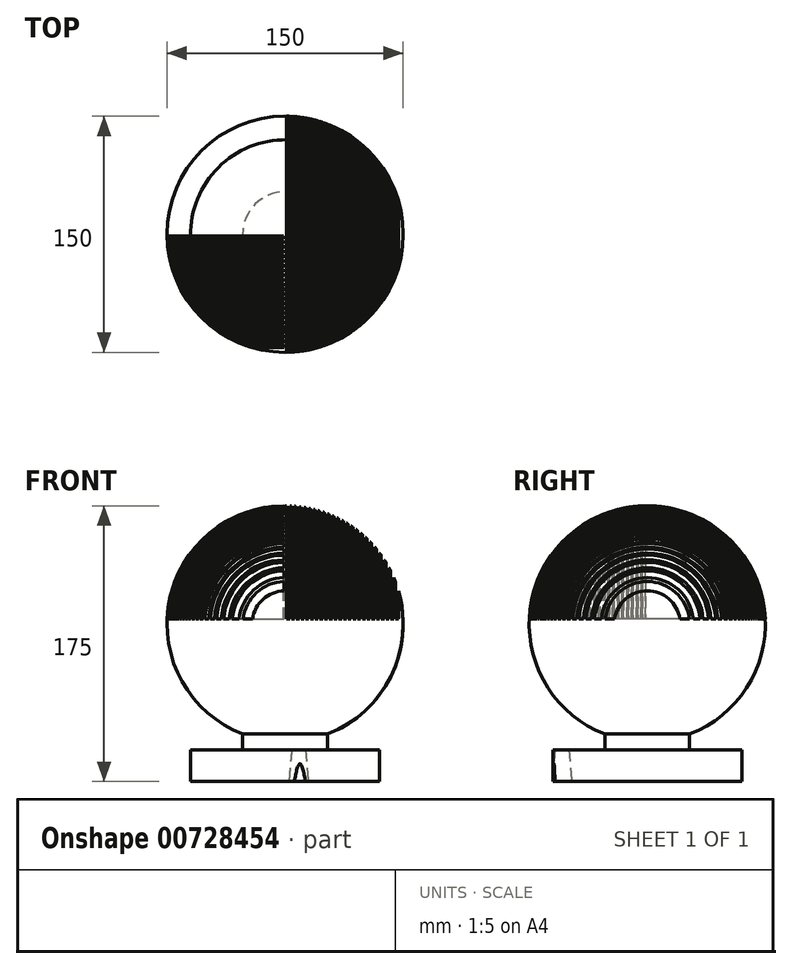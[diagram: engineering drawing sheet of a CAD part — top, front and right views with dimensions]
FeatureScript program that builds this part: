
annotation { "Feature Type Name" : "Feature", "Feature Type Description" : "" }
export const myFeature = defineFeature(function(context is Context, id is Id, definition is map)
    precondition{}
    {
        {
            var Q0;
            Q0=qCreatedBy(makeId("Front.planeOp"),FACE);
            var sketch = newSketch(context, id + "F0", { "sketchPlane" : qUnion([Q0])});
            skArc(sketch, "E0", {"start": v(26.93, -70) * mm, "mid": v(73.74, 13.7) * mm, "end": v(0, 75) * mm});
            skLineSegment(sketch, "E1", {"start": v(0, 75) * mm, "end": v(0, -100) * mm});
            skLineSegment(sketch, "E2", {"start": v(0, -100) * mm, "end": v(60, -100) * mm});
            skLineSegment(sketch, "E3", {"start": v(60, -100) * mm, "end": v(60, -80) * mm});
            skLineSegment(sketch, "E4", {"start": v(60, -80) * mm, "end": v(26.93, -80) * mm});
            skLineSegment(sketch, "E5", {"start": v(26.93, -70) * mm, "end": v(26.93, -80) * mm});
            skPoint(sketch, "E6.orphan", {"position": v(0, 81.47) * mm});
            skSolve(sketch);
        }
        {
            var Q0;
            Q0=makeQuery(id+"F0.imprint","IMPRINT",FACE,{"disambiguationData":[TD([[makeQuery(id+"F0.imprint","IMPRINT",EDGE,{"derivedFrom":sQuery(id+"F0.wireOp",EDGE,"E0")}),1.0]])]});
            var Q1;
            Q1=sQuery(id+"F0.wireOp",EDGE,"E1");
            revolve(context, id + "F1", {"surfaceOperationType" : NewSurfaceOperationType.NEW, "entities" : qUnion([Q0]), "axis" : qUnion([Q1]), "revolveType" : RevolveType.FULL});
        }
        {
            var Q0;
            Q0=qCreatedBy(makeId("Top.planeOp"),FACE);
            cPlane(context, id + "F2", {"entities" : qUnion([Q0]), "cplaneType" : CPlaneType.OFFSET, "offset" : 75 * mm, "width" : 150 * mm, "height" : 150 * mm});
        }
        {
            var Q0;
            Q0=qCreatedBy(id+"F2.planeOp",FACE);
            var sketch = newSketch(context, id + "F3", { "sketchPlane" : qUnion([Q0])});
            skLineSegment(sketch, "E7.bottom", {"start": v(1, 100) * mm, "end": v(3, 100) * mm});
            skLineSegment(sketch, "E7.top", {"start": v(1, -80) * mm, "end": v(3, -80) * mm});
            skLineSegment(sketch, "E7.left", {"start": v(1, 100) * mm, "end": v(1, -80) * mm});
            skLineSegment(sketch, "E7.right", {"start": v(3, 100) * mm, "end": v(3, -80) * mm});
            skLineSegment(sketch, "E8.1.0.0", {"start": v(6, 100) * mm, "end": v(6, -80) * mm});
            skLineSegment(sketch, "E8.1.0.1", {"start": v(4, 100) * mm, "end": v(4, -80) * mm});
            skLineSegment(sketch, "E8.1.0.2", {"start": v(4, -80) * mm, "end": v(6, -80) * mm});
            skLineSegment(sketch, "E8.1.0.3", {"start": v(4, 100) * mm, "end": v(6, 100) * mm});
            skLineSegment(sketch, "E8.2.0.0", {"start": v(9, 100) * mm, "end": v(9, -80) * mm});
            skLineSegment(sketch, "E8.2.0.1", {"start": v(7, 100) * mm, "end": v(7, -80) * mm});
            skLineSegment(sketch, "E8.2.0.2", {"start": v(7, -80) * mm, "end": v(9, -80) * mm});
            skLineSegment(sketch, "E8.2.0.3", {"start": v(7, 100) * mm, "end": v(9, 100) * mm});
            skLineSegment(sketch, "E8.3.0.0", {"start": v(12, 100) * mm, "end": v(12, -80) * mm});
            skLineSegment(sketch, "E8.3.0.1", {"start": v(10, 100) * mm, "end": v(10, -80) * mm});
            skLineSegment(sketch, "E8.3.0.2", {"start": v(10, -80) * mm, "end": v(12, -80) * mm});
            skLineSegment(sketch, "E8.3.0.3", {"start": v(10, 100) * mm, "end": v(12, 100) * mm});
            skLineSegment(sketch, "E8.4.0.0", {"start": v(15, 100) * mm, "end": v(15, -80) * mm});
            skLineSegment(sketch, "E8.4.0.1", {"start": v(13, 100) * mm, "end": v(13, -80) * mm});
            skLineSegment(sketch, "E8.4.0.2", {"start": v(13, -80) * mm, "end": v(15, -80) * mm});
            skLineSegment(sketch, "E8.4.0.3", {"start": v(13, 100) * mm, "end": v(15, 100) * mm});
            skLineSegment(sketch, "E8.5.0.0", {"start": v(18, 100) * mm, "end": v(18, -80) * mm});
            skLineSegment(sketch, "E8.5.0.1", {"start": v(16, 100) * mm, "end": v(16, -80) * mm});
            skLineSegment(sketch, "E8.5.0.2", {"start": v(16, -80) * mm, "end": v(18, -80) * mm});
            skLineSegment(sketch, "E8.5.0.3", {"start": v(16, 100) * mm, "end": v(18, 100) * mm});
            skLineSegment(sketch, "E8.6.0.0", {"start": v(21, 100) * mm, "end": v(21, -80) * mm});
            skLineSegment(sketch, "E8.6.0.1", {"start": v(19, 100) * mm, "end": v(19, -80) * mm});
            skLineSegment(sketch, "E8.6.0.2", {"start": v(19, -80) * mm, "end": v(21, -80) * mm});
            skLineSegment(sketch, "E8.6.0.3", {"start": v(19, 100) * mm, "end": v(21, 100) * mm});
            skLineSegment(sketch, "E8.7.0.0", {"start": v(24, 100) * mm, "end": v(24, -80) * mm});
            skLineSegment(sketch, "E8.7.0.1", {"start": v(22, 100) * mm, "end": v(22, -80) * mm});
            skLineSegment(sketch, "E8.7.0.2", {"start": v(22, -80) * mm, "end": v(24, -80) * mm});
            skLineSegment(sketch, "E8.7.0.3", {"start": v(22, 100) * mm, "end": v(24, 100) * mm});
            skLineSegment(sketch, "E8.8.0.0", {"start": v(27, 100) * mm, "end": v(27, -80) * mm});
            skLineSegment(sketch, "E8.8.0.1", {"start": v(25, 100) * mm, "end": v(25, -80) * mm});
            skLineSegment(sketch, "E8.8.0.2", {"start": v(25, -80) * mm, "end": v(27, -80) * mm});
            skLineSegment(sketch, "E8.8.0.3", {"start": v(25, 100) * mm, "end": v(27, 100) * mm});
            skLineSegment(sketch, "E8.9.0.0", {"start": v(30, 100) * mm, "end": v(30, -80) * mm});
            skLineSegment(sketch, "E8.9.0.1", {"start": v(28, 100) * mm, "end": v(28, -80) * mm});
            skLineSegment(sketch, "E8.9.0.2", {"start": v(28, -80) * mm, "end": v(30, -80) * mm});
            skLineSegment(sketch, "E8.9.0.3", {"start": v(28, 100) * mm, "end": v(30, 100) * mm});
            skLineSegment(sketch, "E8.10.0.0", {"start": v(33, 100) * mm, "end": v(33, -80) * mm});
            skLineSegment(sketch, "E8.10.0.1", {"start": v(31, 100) * mm, "end": v(31, -80) * mm});
            skLineSegment(sketch, "E8.10.0.2", {"start": v(31, -80) * mm, "end": v(33, -80) * mm});
            skLineSegment(sketch, "E8.10.0.3", {"start": v(31, 100) * mm, "end": v(33, 100) * mm});
            skLineSegment(sketch, "E8.11.0.0", {"start": v(36, 100) * mm, "end": v(36, -80) * mm});
            skLineSegment(sketch, "E8.11.0.1", {"start": v(34, 100) * mm, "end": v(34, -80) * mm});
            skLineSegment(sketch, "E8.11.0.2", {"start": v(34, -80) * mm, "end": v(36, -80) * mm});
            skLineSegment(sketch, "E8.11.0.3", {"start": v(34, 100) * mm, "end": v(36, 100) * mm});
            skLineSegment(sketch, "E8.12.0.0", {"start": v(39, 100) * mm, "end": v(39, -80) * mm});
            skLineSegment(sketch, "E8.12.0.1", {"start": v(37, 100) * mm, "end": v(37, -80) * mm});
            skLineSegment(sketch, "E8.12.0.2", {"start": v(37, -80) * mm, "end": v(39, -80) * mm});
            skLineSegment(sketch, "E8.12.0.3", {"start": v(37, 100) * mm, "end": v(39, 100) * mm});
            skLineSegment(sketch, "E8.13.0.0", {"start": v(42, 100) * mm, "end": v(42, -80) * mm});
            skLineSegment(sketch, "E8.13.0.1", {"start": v(40, 100) * mm, "end": v(40, -80) * mm});
            skLineSegment(sketch, "E8.13.0.2", {"start": v(40, -80) * mm, "end": v(42, -80) * mm});
            skLineSegment(sketch, "E8.13.0.3", {"start": v(40, 100) * mm, "end": v(42, 100) * mm});
            skLineSegment(sketch, "E8.14.0.0", {"start": v(45, 100) * mm, "end": v(45, -80) * mm});
            skLineSegment(sketch, "E8.14.0.1", {"start": v(43, 100) * mm, "end": v(43, -80) * mm});
            skLineSegment(sketch, "E8.14.0.2", {"start": v(43, -80) * mm, "end": v(45, -80) * mm});
            skLineSegment(sketch, "E8.14.0.3", {"start": v(43, 100) * mm, "end": v(45, 100) * mm});
            skLineSegment(sketch, "E8.15.0.0", {"start": v(48, 100) * mm, "end": v(48, -80) * mm});
            skLineSegment(sketch, "E8.15.0.1", {"start": v(46, 100) * mm, "end": v(46, -80) * mm});
            skLineSegment(sketch, "E8.15.0.2", {"start": v(46, -80) * mm, "end": v(48, -80) * mm});
            skLineSegment(sketch, "E8.15.0.3", {"start": v(46, 100) * mm, "end": v(48, 100) * mm});
            skLineSegment(sketch, "E8.16.0.0", {"start": v(51, 100) * mm, "end": v(51, -80) * mm});
            skLineSegment(sketch, "E8.16.0.1", {"start": v(49, 100) * mm, "end": v(49, -80) * mm});
            skLineSegment(sketch, "E8.16.0.2", {"start": v(49, -80) * mm, "end": v(51, -80) * mm});
            skLineSegment(sketch, "E8.16.0.3", {"start": v(49, 100) * mm, "end": v(51, 100) * mm});
            skLineSegment(sketch, "E8.17.0.0", {"start": v(54, 100) * mm, "end": v(54, -80) * mm});
            skLineSegment(sketch, "E8.17.0.1", {"start": v(52, 100) * mm, "end": v(52, -80) * mm});
            skLineSegment(sketch, "E8.17.0.2", {"start": v(52, -80) * mm, "end": v(54, -80) * mm});
            skLineSegment(sketch, "E8.17.0.3", {"start": v(52, 100) * mm, "end": v(54, 100) * mm});
            skLineSegment(sketch, "E8.direction1", {"start": v(1, -80) * mm, "end": v(4, -80) * mm, "construction": true});
            skLineSegment(sketch, "E9.0.18.0", {"start": v(57, 100) * mm, "end": v(57, -80) * mm});
            skLineSegment(sketch, "E9.3.18.0", {"start": v(55, 100) * mm, "end": v(55, -80) * mm});
            skLineSegment(sketch, "E9.6.18.0", {"start": v(55, -80) * mm, "end": v(57, -80) * mm});
            skLineSegment(sketch, "E9.9.18.0", {"start": v(55, 100) * mm, "end": v(57, 100) * mm});
            skLineSegment(sketch, "E9.0.19.0", {"start": v(60, 100) * mm, "end": v(60, -80) * mm});
            skLineSegment(sketch, "E9.3.19.0", {"start": v(58, 100) * mm, "end": v(58, -80) * mm});
            skLineSegment(sketch, "E9.6.19.0", {"start": v(58, -80) * mm, "end": v(60, -80) * mm});
            skLineSegment(sketch, "E9.9.19.0", {"start": v(58, 100) * mm, "end": v(60, 100) * mm});
            skLineSegment(sketch, "E9.0.20.0", {"start": v(63, 100) * mm, "end": v(63, -80) * mm});
            skLineSegment(sketch, "E9.3.20.0", {"start": v(61, 100) * mm, "end": v(61, -80) * mm});
            skLineSegment(sketch, "E9.6.20.0", {"start": v(61, -80) * mm, "end": v(63, -80) * mm});
            skLineSegment(sketch, "E9.9.20.0", {"start": v(61, 100) * mm, "end": v(63, 100) * mm});
            skLineSegment(sketch, "E9.0.21.0", {"start": v(66, 100) * mm, "end": v(66, -80) * mm});
            skLineSegment(sketch, "E9.3.21.0", {"start": v(64, 100) * mm, "end": v(64, -80) * mm});
            skLineSegment(sketch, "E9.6.21.0", {"start": v(64, -80) * mm, "end": v(66, -80) * mm});
            skLineSegment(sketch, "E9.9.21.0", {"start": v(64, 100) * mm, "end": v(66, 100) * mm});
            skLineSegment(sketch, "E9.0.22.0", {"start": v(69, 100) * mm, "end": v(69, -80) * mm});
            skLineSegment(sketch, "E9.3.22.0", {"start": v(67, 100) * mm, "end": v(67, -80) * mm});
            skLineSegment(sketch, "E9.6.22.0", {"start": v(67, -80) * mm, "end": v(69, -80) * mm});
            skLineSegment(sketch, "E9.9.22.0", {"start": v(67, 100) * mm, "end": v(69, 100) * mm});
            skLineSegment(sketch, "E9.0.23.0", {"start": v(72, 100) * mm, "end": v(72, -80) * mm});
            skLineSegment(sketch, "E9.3.23.0", {"start": v(70, 100) * mm, "end": v(70, -80) * mm});
            skLineSegment(sketch, "E9.6.23.0", {"start": v(70, -80) * mm, "end": v(72, -80) * mm});
            skLineSegment(sketch, "E9.9.23.0", {"start": v(70, 100) * mm, "end": v(72, 100) * mm});
            skSolve(sketch);
        }
        {
            var Q0;
            Q0=makeQuery(id+"F3.imprint","IMPRINT",FACE,{"disambiguationData":[TD([[makeQuery(id+"F3.imprint","IMPRINT",EDGE,{"derivedFrom":sQuery(id+"F3.wireOp",EDGE,"E9.0.23.0")}),-1.0]])]});
            var Q1;
            Q1=makeQuery(id+"F3.imprint","IMPRINT",FACE,{"disambiguationData":[TD([[makeQuery(id+"F3.imprint","IMPRINT",EDGE,{"derivedFrom":sQuery(id+"F3.wireOp",EDGE,"E9.0.18.0")}),-1.0]])]});
            var Q2;
            Q2=makeQuery(id+"F3.imprint","IMPRINT",FACE,{"disambiguationData":[TD([[makeQuery(id+"F3.imprint","IMPRINT",EDGE,{"derivedFrom":sQuery(id+"F3.wireOp",EDGE,"E8.15.0.0")}),-1.0]])]});
            var Q3;
            Q3=makeQuery(id+"F3.imprint","IMPRINT",FACE,{"disambiguationData":[TD([[makeQuery(id+"F3.imprint","IMPRINT",EDGE,{"derivedFrom":sQuery(id+"F3.wireOp",EDGE,"E8.13.0.0")}),-1.0]])]});
            var Q4;
            Q4=makeQuery(id+"F3.imprint","IMPRINT",FACE,{"disambiguationData":[TD([[makeQuery(id+"F3.imprint","IMPRINT",EDGE,{"derivedFrom":sQuery(id+"F3.wireOp",EDGE,"E8.14.0.0")}),-1.0]])]});
            var Q5;
            Q5=makeQuery(id+"F3.imprint","IMPRINT",FACE,{"disambiguationData":[TD([[makeQuery(id+"F3.imprint","IMPRINT",EDGE,{"derivedFrom":sQuery(id+"F3.wireOp",EDGE,"E7.bottom")}),-1.0]])]});
            var Q6;
            Q6=makeQuery(id+"F3.imprint","IMPRINT",FACE,{"disambiguationData":[TD([[makeQuery(id+"F3.imprint","IMPRINT",EDGE,{"derivedFrom":sQuery(id+"F3.wireOp",EDGE,"E8.2.0.0")}),-1.0]])]});
            var Q7;
            Q7=makeQuery(id+"F3.imprint","IMPRINT",FACE,{"disambiguationData":[TD([[makeQuery(id+"F3.imprint","IMPRINT",EDGE,{"derivedFrom":sQuery(id+"F3.wireOp",EDGE,"E8.3.0.0")}),-1.0]])]});
            var Q8;
            Q8=makeQuery(id+"F3.imprint","IMPRINT",FACE,{"disambiguationData":[TD([[makeQuery(id+"F3.imprint","IMPRINT",EDGE,{"derivedFrom":sQuery(id+"F3.wireOp",EDGE,"E8.4.0.0")}),-1.0]])]});
            var Q9;
            Q9=makeQuery(id+"F3.imprint","IMPRINT",FACE,{"disambiguationData":[TD([[makeQuery(id+"F3.imprint","IMPRINT",EDGE,{"derivedFrom":sQuery(id+"F3.wireOp",EDGE,"E8.5.0.0")}),-1.0]])]});
            var Q10;
            Q10=makeQuery(id+"F3.imprint","IMPRINT",FACE,{"disambiguationData":[TD([[makeQuery(id+"F3.imprint","IMPRINT",EDGE,{"derivedFrom":sQuery(id+"F3.wireOp",EDGE,"E8.7.0.0")}),-1.0]])]});
            var Q11;
            Q11=makeQuery(id+"F3.imprint","IMPRINT",FACE,{"disambiguationData":[TD([[makeQuery(id+"F3.imprint","IMPRINT",EDGE,{"derivedFrom":sQuery(id+"F3.wireOp",EDGE,"E8.9.0.0")}),-1.0]])]});
            var Q12;
            Q12=makeQuery(id+"F3.imprint","IMPRINT",FACE,{"disambiguationData":[TD([[makeQuery(id+"F3.imprint","IMPRINT",EDGE,{"derivedFrom":sQuery(id+"F3.wireOp",EDGE,"E8.11.0.0")}),-1.0]])]});
            var Q13;
            Q13=makeQuery(id+"F3.imprint","IMPRINT",FACE,{"disambiguationData":[TD([[makeQuery(id+"F3.imprint","IMPRINT",EDGE,{"derivedFrom":sQuery(id+"F3.wireOp",EDGE,"E8.12.0.0")}),-1.0]])]});
            var Q14;
            Q14=makeQuery(id+"F3.imprint","IMPRINT",FACE,{"disambiguationData":[TD([[makeQuery(id+"F3.imprint","IMPRINT",EDGE,{"derivedFrom":sQuery(id+"F3.wireOp",EDGE,"E9.0.20.0")}),-1.0]])]});
            var Q15;
            Q15=makeQuery(id+"F3.imprint","IMPRINT",FACE,{"disambiguationData":[TD([[makeQuery(id+"F3.imprint","IMPRINT",EDGE,{"derivedFrom":sQuery(id+"F3.wireOp",EDGE,"E8.16.0.0")}),-1.0]])]});
            var Q16;
            Q16=makeQuery(id+"F3.imprint","IMPRINT",FACE,{"disambiguationData":[TD([[makeQuery(id+"F3.imprint","IMPRINT",EDGE,{"derivedFrom":sQuery(id+"F3.wireOp",EDGE,"E9.0.22.0")}),-1.0]])]});
            var Q17;
            Q17=makeQuery(id+"F3.imprint","IMPRINT",FACE,{"disambiguationData":[TD([[makeQuery(id+"F3.imprint","IMPRINT",EDGE,{"derivedFrom":sQuery(id+"F3.wireOp",EDGE,"E8.17.0.0")}),-1.0]])]});
            var Q18;
            Q18=makeQuery(id+"F3.imprint","IMPRINT",FACE,{"disambiguationData":[TD([[makeQuery(id+"F3.imprint","IMPRINT",EDGE,{"derivedFrom":sQuery(id+"F3.wireOp",EDGE,"E9.0.19.0")}),-1.0]])]});
            var Q19;
            Q19=makeQuery(id+"F3.imprint","IMPRINT",FACE,{"disambiguationData":[TD([[makeQuery(id+"F3.imprint","IMPRINT",EDGE,{"derivedFrom":sQuery(id+"F3.wireOp",EDGE,"E8.1.0.0")}),-1.0]])]});
            var Q20;
            Q20=makeQuery(id+"F3.imprint","IMPRINT",FACE,{"disambiguationData":[TD([[makeQuery(id+"F3.imprint","IMPRINT",EDGE,{"derivedFrom":sQuery(id+"F3.wireOp",EDGE,"E8.6.0.0")}),-1.0]])]});
            var Q21;
            Q21=makeQuery(id+"F3.imprint","IMPRINT",FACE,{"disambiguationData":[TD([[makeQuery(id+"F3.imprint","IMPRINT",EDGE,{"derivedFrom":sQuery(id+"F3.wireOp",EDGE,"E8.8.0.0")}),-1.0]])]});
            var Q22;
            Q22=makeQuery(id+"F3.imprint","IMPRINT",FACE,{"disambiguationData":[TD([[makeQuery(id+"F3.imprint","IMPRINT",EDGE,{"derivedFrom":sQuery(id+"F3.wireOp",EDGE,"E8.10.0.0")}),-1.0]])]});
            var Q23;
            Q23=makeQuery(id+"F3.imprint","IMPRINT",FACE,{"disambiguationData":[TD([[makeQuery(id+"F3.imprint","IMPRINT",EDGE,{"derivedFrom":sQuery(id+"F3.wireOp",EDGE,"E9.0.21.0")}),-1.0]])]});
            extrude(context, id + "F4", {"entities" : qUnion([Q0, Q1, Q2, Q3, Q4, Q5, Q6, Q7, Q8, Q9, Q10, Q11, Q12, Q13, Q14, Q15, Q16, Q17, Q18, Q19, Q20, Q21, Q22, Q23]), "operationType" : NewBodyOperationType.REMOVE, "oppositeDirection" : true, "depth" : 72 * mm, "offsetDistance" : 25 * mm});
        }
        {
            var Q0;
            Q0=qCreatedBy(id+"F2.planeOp",FACE);
            var sketch = newSketch(context, id + "F5", { "sketchPlane" : qUnion([Q0])});
            skLineSegment(sketch, "E10.bottom", {"start": v(-81, -1) * mm, "end": v(-1, -1) * mm});
            skLineSegment(sketch, "E10.top", {"start": v(-81, -3) * mm, "end": v(-1, -3) * mm});
            skLineSegment(sketch, "E10.left", {"start": v(-81, -1) * mm, "end": v(-81, -3) * mm});
            skLineSegment(sketch, "E10.right", {"start": v(-1, -1) * mm, "end": v(-1, -3) * mm});
            skLineSegment(sketch, "E11.1.0.0", {"start": v(-80.99, -4) * mm, "end": v(-0.99, -4) * mm});
            skLineSegment(sketch, "E11.1.0.1", {"start": v(-80.99, -6) * mm, "end": v(-0.99, -6) * mm});
            skLineSegment(sketch, "E11.1.0.2", {"start": v(-80.99, -4) * mm, "end": v(-80.99, -6) * mm});
            skLineSegment(sketch, "E11.1.0.3", {"start": v(-0.99, -4) * mm, "end": v(-0.99, -6) * mm});
            skLineSegment(sketch, "E11.2.0.0", {"start": v(-80.97, -7) * mm, "end": v(-0.97, -7) * mm});
            skLineSegment(sketch, "E11.2.0.1", {"start": v(-80.97, -9) * mm, "end": v(-0.97, -9) * mm});
            skLineSegment(sketch, "E11.2.0.2", {"start": v(-80.97, -7) * mm, "end": v(-80.97, -9) * mm});
            skLineSegment(sketch, "E11.2.0.3", {"start": v(-0.97, -7) * mm, "end": v(-0.97, -9) * mm});
            skLineSegment(sketch, "E11.3.0.0", {"start": v(-80.96, -10) * mm, "end": v(-0.96, -10) * mm});
            skLineSegment(sketch, "E11.3.0.1", {"start": v(-80.96, -12) * mm, "end": v(-0.96, -12) * mm});
            skLineSegment(sketch, "E11.3.0.2", {"start": v(-80.96, -10) * mm, "end": v(-80.96, -12) * mm});
            skLineSegment(sketch, "E11.3.0.3", {"start": v(-0.96, -10) * mm, "end": v(-0.96, -12) * mm});
            skLineSegment(sketch, "E11.4.0.0", {"start": v(-80.94, -13) * mm, "end": v(-0.94, -13) * mm});
            skLineSegment(sketch, "E11.4.0.1", {"start": v(-80.94, -15) * mm, "end": v(-0.94, -15) * mm});
            skLineSegment(sketch, "E11.4.0.2", {"start": v(-80.94, -13) * mm, "end": v(-80.94, -15) * mm});
            skLineSegment(sketch, "E11.4.0.3", {"start": v(-0.94, -13) * mm, "end": v(-0.94, -15) * mm});
            skLineSegment(sketch, "E11.5.0.0", {"start": v(-80.93, -16) * mm, "end": v(-0.93, -16) * mm});
            skLineSegment(sketch, "E11.5.0.1", {"start": v(-80.93, -18) * mm, "end": v(-0.93, -18) * mm});
            skLineSegment(sketch, "E11.5.0.2", {"start": v(-80.93, -16) * mm, "end": v(-80.93, -18) * mm});
            skLineSegment(sketch, "E11.5.0.3", {"start": v(-0.93, -16) * mm, "end": v(-0.93, -18) * mm});
            skLineSegment(sketch, "E11.6.0.0", {"start": v(-80.92, -19) * mm, "end": v(-0.92, -19) * mm});
            skLineSegment(sketch, "E11.6.0.1", {"start": v(-80.92, -21) * mm, "end": v(-0.92, -21) * mm});
            skLineSegment(sketch, "E11.6.0.2", {"start": v(-80.92, -19) * mm, "end": v(-80.92, -21) * mm});
            skLineSegment(sketch, "E11.6.0.3", {"start": v(-0.92, -19) * mm, "end": v(-0.92, -21) * mm});
            skLineSegment(sketch, "E11.7.0.0", {"start": v(-80.9, -22) * mm, "end": v(-0.9, -22) * mm});
            skLineSegment(sketch, "E11.7.0.1", {"start": v(-80.9, -24) * mm, "end": v(-0.9, -24) * mm});
            skLineSegment(sketch, "E11.7.0.2", {"start": v(-80.9, -22) * mm, "end": v(-80.9, -24) * mm});
            skLineSegment(sketch, "E11.7.0.3", {"start": v(-0.9, -22) * mm, "end": v(-0.9, -24) * mm});
            skLineSegment(sketch, "E11.8.0.0", {"start": v(-80.89, -25) * mm, "end": v(-0.89, -25) * mm});
            skLineSegment(sketch, "E11.8.0.1", {"start": v(-80.89, -27) * mm, "end": v(-0.89, -27) * mm});
            skLineSegment(sketch, "E11.8.0.2", {"start": v(-80.89, -25) * mm, "end": v(-80.89, -27) * mm});
            skLineSegment(sketch, "E11.8.0.3", {"start": v(-0.89, -25) * mm, "end": v(-0.89, -27) * mm});
            skLineSegment(sketch, "E11.9.0.0", {"start": v(-80.87, -28) * mm, "end": v(-0.87, -28) * mm});
            skLineSegment(sketch, "E11.9.0.1", {"start": v(-80.87, -30) * mm, "end": v(-0.87, -30) * mm});
            skLineSegment(sketch, "E11.9.0.2", {"start": v(-80.87, -28) * mm, "end": v(-80.87, -30) * mm});
            skLineSegment(sketch, "E11.9.0.3", {"start": v(-0.87, -28) * mm, "end": v(-0.87, -30) * mm});
            skLineSegment(sketch, "E11.10.0.0", {"start": v(-80.86, -31) * mm, "end": v(-0.86, -31) * mm});
            skLineSegment(sketch, "E11.10.0.1", {"start": v(-80.86, -33) * mm, "end": v(-0.86, -33) * mm});
            skLineSegment(sketch, "E11.10.0.2", {"start": v(-80.86, -31) * mm, "end": v(-80.86, -33) * mm});
            skLineSegment(sketch, "E11.10.0.3", {"start": v(-0.86, -31) * mm, "end": v(-0.86, -33) * mm});
            skLineSegment(sketch, "E11.11.0.0", {"start": v(-80.85, -34) * mm, "end": v(-0.85, -34) * mm});
            skLineSegment(sketch, "E11.11.0.1", {"start": v(-80.85, -36) * mm, "end": v(-0.85, -36) * mm});
            skLineSegment(sketch, "E11.11.0.2", {"start": v(-80.85, -34) * mm, "end": v(-80.85, -36) * mm});
            skLineSegment(sketch, "E11.11.0.3", {"start": v(-0.85, -34) * mm, "end": v(-0.85, -36) * mm});
            skLineSegment(sketch, "E11.12.0.0", {"start": v(-80.83, -37) * mm, "end": v(-0.83, -37) * mm});
            skLineSegment(sketch, "E11.12.0.1", {"start": v(-80.83, -39) * mm, "end": v(-0.83, -39) * mm});
            skLineSegment(sketch, "E11.12.0.2", {"start": v(-80.83, -37) * mm, "end": v(-80.83, -39) * mm});
            skLineSegment(sketch, "E11.12.0.3", {"start": v(-0.83, -37) * mm, "end": v(-0.83, -39) * mm});
            skLineSegment(sketch, "E11.13.0.0", {"start": v(-80.82, -40) * mm, "end": v(-0.82, -40) * mm});
            skLineSegment(sketch, "E11.13.0.1", {"start": v(-80.82, -42) * mm, "end": v(-0.82, -42) * mm});
            skLineSegment(sketch, "E11.13.0.2", {"start": v(-80.82, -40) * mm, "end": v(-80.82, -42) * mm});
            skLineSegment(sketch, "E11.13.0.3", {"start": v(-0.82, -40) * mm, "end": v(-0.82, -42) * mm});
            skLineSegment(sketch, "E11.14.0.0", {"start": v(-80.8, -43) * mm, "end": v(-0.8, -43) * mm});
            skLineSegment(sketch, "E11.14.0.1", {"start": v(-80.8, -45) * mm, "end": v(-0.8, -45) * mm});
            skLineSegment(sketch, "E11.14.0.2", {"start": v(-80.8, -43) * mm, "end": v(-80.8, -45) * mm});
            skLineSegment(sketch, "E11.14.0.3", {"start": v(-0.8, -43) * mm, "end": v(-0.8, -45) * mm});
            skLineSegment(sketch, "E11.15.0.0", {"start": v(-80.8, -46) * mm, "end": v(-0.8, -46) * mm});
            skLineSegment(sketch, "E11.15.0.1", {"start": v(-80.8, -48) * mm, "end": v(-0.8, -48) * mm});
            skLineSegment(sketch, "E11.15.0.2", {"start": v(-80.8, -46) * mm, "end": v(-80.8, -48) * mm});
            skLineSegment(sketch, "E11.15.0.3", {"start": v(-0.8, -46) * mm, "end": v(-0.8, -48) * mm});
            skLineSegment(sketch, "E11.16.0.0", {"start": v(-80.78, -49) * mm, "end": v(-0.78, -49) * mm});
            skLineSegment(sketch, "E11.16.0.1", {"start": v(-80.78, -51) * mm, "end": v(-0.78, -51) * mm});
            skLineSegment(sketch, "E11.16.0.2", {"start": v(-80.78, -49) * mm, "end": v(-80.78, -51) * mm});
            skLineSegment(sketch, "E11.16.0.3", {"start": v(-0.78, -49) * mm, "end": v(-0.78, -51) * mm});
            skLineSegment(sketch, "E11.17.0.0", {"start": v(-80.76, -52) * mm, "end": v(-0.76, -52) * mm});
            skLineSegment(sketch, "E11.17.0.1", {"start": v(-80.76, -54) * mm, "end": v(-0.76, -54) * mm});
            skLineSegment(sketch, "E11.17.0.2", {"start": v(-80.76, -52) * mm, "end": v(-80.76, -54) * mm});
            skLineSegment(sketch, "E11.17.0.3", {"start": v(-0.76, -52) * mm, "end": v(-0.76, -54) * mm});
            skLineSegment(sketch, "E11.18.0.0", {"start": v(-80.75, -55) * mm, "end": v(-0.75, -55) * mm});
            skLineSegment(sketch, "E11.18.0.1", {"start": v(-80.75, -57) * mm, "end": v(-0.75, -57) * mm});
            skLineSegment(sketch, "E11.18.0.2", {"start": v(-80.75, -55) * mm, "end": v(-80.75, -57) * mm});
            skLineSegment(sketch, "E11.18.0.3", {"start": v(-0.75, -55) * mm, "end": v(-0.75, -57) * mm});
            skLineSegment(sketch, "E11.19.0.0", {"start": v(-80.74, -58) * mm, "end": v(-0.74, -58) * mm});
            skLineSegment(sketch, "E11.19.0.1", {"start": v(-80.74, -60) * mm, "end": v(-0.74, -60) * mm});
            skLineSegment(sketch, "E11.19.0.2", {"start": v(-80.74, -58) * mm, "end": v(-80.74, -60) * mm});
            skLineSegment(sketch, "E11.19.0.3", {"start": v(-0.74, -58) * mm, "end": v(-0.74, -60) * mm});
            skLineSegment(sketch, "E11.20.0.0", {"start": v(-80.72, -61) * mm, "end": v(-0.72, -61) * mm});
            skLineSegment(sketch, "E11.20.0.1", {"start": v(-80.72, -63) * mm, "end": v(-0.72, -63) * mm});
            skLineSegment(sketch, "E11.20.0.2", {"start": v(-80.72, -61) * mm, "end": v(-80.72, -63) * mm});
            skLineSegment(sketch, "E11.20.0.3", {"start": v(-0.72, -61) * mm, "end": v(-0.72, -63) * mm});
            skLineSegment(sketch, "E11.21.0.0", {"start": v(-80.7, -64) * mm, "end": v(-0.7, -64) * mm});
            skLineSegment(sketch, "E11.21.0.1", {"start": v(-80.7, -66) * mm, "end": v(-0.7, -66) * mm});
            skLineSegment(sketch, "E11.21.0.2", {"start": v(-80.7, -64) * mm, "end": v(-80.7, -66) * mm});
            skLineSegment(sketch, "E11.21.0.3", {"start": v(-0.7, -64) * mm, "end": v(-0.7, -66) * mm});
            skLineSegment(sketch, "E11.22.0.0", {"start": v(-80.7, -67) * mm, "end": v(-0.7, -67) * mm});
            skLineSegment(sketch, "E11.22.0.1", {"start": v(-80.7, -69) * mm, "end": v(-0.7, -69) * mm});
            skLineSegment(sketch, "E11.22.0.2", {"start": v(-80.7, -67) * mm, "end": v(-80.7, -69) * mm});
            skLineSegment(sketch, "E11.22.0.3", {"start": v(-0.7, -67) * mm, "end": v(-0.7, -69) * mm});
            skLineSegment(sketch, "E11.23.0.0", {"start": v(-80.68, -70) * mm, "end": v(-0.68, -70) * mm});
            skLineSegment(sketch, "E11.23.0.1", {"start": v(-80.68, -72) * mm, "end": v(-0.68, -72) * mm});
            skLineSegment(sketch, "E11.23.0.2", {"start": v(-80.68, -70) * mm, "end": v(-80.68, -72) * mm});
            skLineSegment(sketch, "E11.23.0.3", {"start": v(-0.68, -70) * mm, "end": v(-0.68, -72) * mm});
            skLineSegment(sketch, "E11.direction1", {"start": v(-81, -3) * mm, "end": v(-80.99, -6) * mm, "construction": true});
            skSolve(sketch);
        }
        {
            var Q0;
            Q0=makeQuery(id+"F5.imprint","IMPRINT",FACE,{"disambiguationData":[TD([[makeQuery(id+"F5.imprint","IMPRINT",EDGE,{"derivedFrom":sQuery(id+"F5.wireOp",EDGE,"E11.18.0.0")}),-1.0]])]});
            var Q1;
            Q1=makeQuery(id+"F5.imprint","IMPRINT",FACE,{"disambiguationData":[TD([[makeQuery(id+"F5.imprint","IMPRINT",EDGE,{"derivedFrom":sQuery(id+"F5.wireOp",EDGE,"E11.22.0.0")}),-1.0]])]});
            var Q2;
            Q2=makeQuery(id+"F5.imprint","IMPRINT",FACE,{"disambiguationData":[TD([[makeQuery(id+"F5.imprint","IMPRINT",EDGE,{"derivedFrom":sQuery(id+"F5.wireOp",EDGE,"E11.9.0.0")}),-1.0]])]});
            var Q3;
            Q3=makeQuery(id+"F5.imprint","IMPRINT",FACE,{"disambiguationData":[TD([[makeQuery(id+"F5.imprint","IMPRINT",EDGE,{"derivedFrom":sQuery(id+"F5.wireOp",EDGE,"E11.12.0.0")}),-1.0]])]});
            var Q4;
            Q4=makeQuery(id+"F5.imprint","IMPRINT",FACE,{"disambiguationData":[TD([[makeQuery(id+"F5.imprint","IMPRINT",EDGE,{"derivedFrom":sQuery(id+"F5.wireOp",EDGE,"E11.13.0.0")}),-1.0]])]});
            var Q5;
            Q5=makeQuery(id+"F5.imprint","IMPRINT",FACE,{"disambiguationData":[TD([[makeQuery(id+"F5.imprint","IMPRINT",EDGE,{"derivedFrom":sQuery(id+"F5.wireOp",EDGE,"E11.15.0.0")}),-1.0]])]});
            var Q6;
            Q6=makeQuery(id+"F5.imprint","IMPRINT",FACE,{"disambiguationData":[TD([[makeQuery(id+"F5.imprint","IMPRINT",EDGE,{"derivedFrom":sQuery(id+"F5.wireOp",EDGE,"E11.14.0.0")}),-1.0]])]});
            var Q7;
            Q7=makeQuery(id+"F5.imprint","IMPRINT",FACE,{"disambiguationData":[TD([[makeQuery(id+"F5.imprint","IMPRINT",EDGE,{"derivedFrom":sQuery(id+"F5.wireOp",EDGE,"E11.6.0.0")}),-1.0]])]});
            var Q8;
            Q8=makeQuery(id+"F5.imprint","IMPRINT",FACE,{"disambiguationData":[TD([[makeQuery(id+"F5.imprint","IMPRINT",EDGE,{"derivedFrom":sQuery(id+"F5.wireOp",EDGE,"E11.20.0.0")}),-1.0]])]});
            var Q9;
            Q9=makeQuery(id+"F5.imprint","IMPRINT",FACE,{"disambiguationData":[TD([[makeQuery(id+"F5.imprint","IMPRINT",EDGE,{"derivedFrom":sQuery(id+"F5.wireOp",EDGE,"E11.19.0.0")}),-1.0]])]});
            var Q10;
            Q10=makeQuery(id+"F5.imprint","IMPRINT",FACE,{"disambiguationData":[TD([[makeQuery(id+"F5.imprint","IMPRINT",EDGE,{"derivedFrom":sQuery(id+"F5.wireOp",EDGE,"E11.16.0.0")}),-1.0]])]});
            var Q11;
            Q11=makeQuery(id+"F5.imprint","IMPRINT",FACE,{"disambiguationData":[TD([[makeQuery(id+"F5.imprint","IMPRINT",EDGE,{"derivedFrom":sQuery(id+"F5.wireOp",EDGE,"E11.7.0.0")}),-1.0]])]});
            var Q12;
            Q12=makeQuery(id+"F5.imprint","IMPRINT",FACE,{"disambiguationData":[TD([[makeQuery(id+"F5.imprint","IMPRINT",EDGE,{"derivedFrom":sQuery(id+"F5.wireOp",EDGE,"E11.11.0.0")}),-1.0]])]});
            var Q13;
            Q13=makeQuery(id+"F5.imprint","IMPRINT",FACE,{"disambiguationData":[TD([[makeQuery(id+"F5.imprint","IMPRINT",EDGE,{"derivedFrom":sQuery(id+"F5.wireOp",EDGE,"E11.21.0.0")}),-1.0]])]});
            var Q14;
            Q14=makeQuery(id+"F5.imprint","IMPRINT",FACE,{"disambiguationData":[TD([[makeQuery(id+"F5.imprint","IMPRINT",EDGE,{"derivedFrom":sQuery(id+"F5.wireOp",EDGE,"E11.17.0.0")}),-1.0]])]});
            var Q15;
            Q15=makeQuery(id+"F5.imprint","IMPRINT",FACE,{"disambiguationData":[TD([[makeQuery(id+"F5.imprint","IMPRINT",EDGE,{"derivedFrom":sQuery(id+"F5.wireOp",EDGE,"E11.2.0.0")}),-1.0]])]});
            var Q16;
            Q16=makeQuery(id+"F5.imprint","IMPRINT",FACE,{"disambiguationData":[TD([[makeQuery(id+"F5.imprint","IMPRINT",EDGE,{"derivedFrom":sQuery(id+"F5.wireOp",EDGE,"E11.1.0.0")}),-1.0]])]});
            var Q17;
            Q17=makeQuery(id+"F5.imprint","IMPRINT",FACE,{"disambiguationData":[TD([[makeQuery(id+"F5.imprint","IMPRINT",EDGE,{"derivedFrom":sQuery(id+"F5.wireOp",EDGE,"E11.3.0.0")}),-1.0]])]});
            var Q18;
            Q18=makeQuery(id+"F5.imprint","IMPRINT",FACE,{"disambiguationData":[TD([[makeQuery(id+"F5.imprint","IMPRINT",EDGE,{"derivedFrom":sQuery(id+"F5.wireOp",EDGE,"E11.5.0.0")}),-1.0]])]});
            var Q19;
            Q19=makeQuery(id+"F5.imprint","IMPRINT",FACE,{"disambiguationData":[TD([[makeQuery(id+"F5.imprint","IMPRINT",EDGE,{"derivedFrom":sQuery(id+"F5.wireOp",EDGE,"E11.4.0.0")}),-1.0]])]});
            var Q20;
            Q20=makeQuery(id+"F5.imprint","IMPRINT",FACE,{"disambiguationData":[TD([[makeQuery(id+"F5.imprint","IMPRINT",EDGE,{"derivedFrom":sQuery(id+"F5.wireOp",EDGE,"E11.10.0.0")}),-1.0]])]});
            var Q21;
            Q21=makeQuery(id+"F5.imprint","IMPRINT",FACE,{"disambiguationData":[TD([[makeQuery(id+"F5.imprint","IMPRINT",EDGE,{"derivedFrom":sQuery(id+"F5.wireOp",EDGE,"E11.23.0.0")}),-1.0]])]});
            var Q22;
            Q22=makeQuery(id+"F5.imprint","IMPRINT",FACE,{"disambiguationData":[TD([[makeQuery(id+"F5.imprint","IMPRINT",EDGE,{"derivedFrom":sQuery(id+"F5.wireOp",EDGE,"E11.8.0.0")}),-1.0]])]});
            var Q23;
            Q23=makeQuery(id+"F5.imprint","IMPRINT",FACE,{"disambiguationData":[TD([[makeQuery(id+"F5.imprint","IMPRINT",EDGE,{"derivedFrom":sQuery(id+"F5.wireOp",EDGE,"E10.bottom")}),-1.0]])]});
            extrude(context, id + "F6", {"entities" : qUnion([Q0, Q1, Q2, Q3, Q4, Q5, Q6, Q7, Q8, Q9, Q10, Q11, Q12, Q13, Q14, Q15, Q16, Q17, Q18, Q19, Q20, Q21, Q22, Q23]), "operationType" : NewBodyOperationType.REMOVE, "oppositeDirection" : true, "depth" : 72 * mm, "offsetDistance" : 25 * mm});
        }
        {
            var Q0;
            Q0=makeQuery(id+"F1.opRevolve","SWEPT_FACE",FACE,{"disambiguationData":[OSD([sQuery(id+"F0.wireOp",EDGE,"E4")])]});
            cPlane(context, id + "F7", {"entities" : qUnion([Q0]), "cplaneType" : CPlaneType.OFFSET, "offset" : 5 * mm, "width" : 150 * mm, "height" : 150 * mm});
        }
        {
            var Q0;
            Q0=qCreatedBy(id+"F7.planeOp",FACE);
            var sketch = newSketch(context, id + "F8", { "sketchPlane" : qUnion([Q0])});
            skCircle(sketch, "E12", {"center": v(8.6, -54.12) * mm, "radius": 4 * mm});
            skSolve(sketch);
        }
        {
            var Q0;
            Q0 = qSketchRegion(id + "F8", true);
            extrude(context, id + "F9", {"entities" : qUnion([Q0]), "operationType" : NewBodyOperationType.REMOVE, "oppositeDirection" : true, "depth" : 36 * mm, "offsetDistance" : 25 * mm, "hasDraft" : true, "draftAngle" : 5 * degree});
        }
    });
